# Revit family: Oberteil V20
name_source: partatom
category: Generic Models
revit_build: Autodesk Revit 2015 (Build: 20140606_1530(x64)
units: mm (PartAtom-declared; Revit-internal decimal feet)

## types (7) — shared parameters
Height = 58 mm  [stored 0.190289 ft]
Length = 18 mm
Manufacturer = OBO Bettermann
Material = PA 66/6 FR HF RAL 9010
Material 2 = PA 66/6 FR HF RAL 2003
URL = http://www.obo-bettermann.com
Width = 45 mm  [stored 0.147638 ft]

## per-type parameters (varying)
| type | GTIN | Manufacturer Art.No. |
| V20-0-75 | 4012196163533 | 5095360 |
| V20-0-150 | 4012196163540 | 5095362 |
| V20-0-280 | 4012196163557 | 5095364 |
| V20-0-320 | 4012196163595 | 5095366 |
| V20-0-385 | 4012196163601 | 5095368 |
| V20-0-440 | 4012196163618 | 5095370 |
| V20-0-550 | 4012196163625 | 5095372 |

note: column(s) folded — value = type name in every type: Article Type

note: [stored X ft] marks values corroborated as IEEE doubles in the binary element streams (Revit-internal decimal feet)

## geometry (parser evidence)
native form markers: Sweep x3
no freeform markers — native parametric forms only
